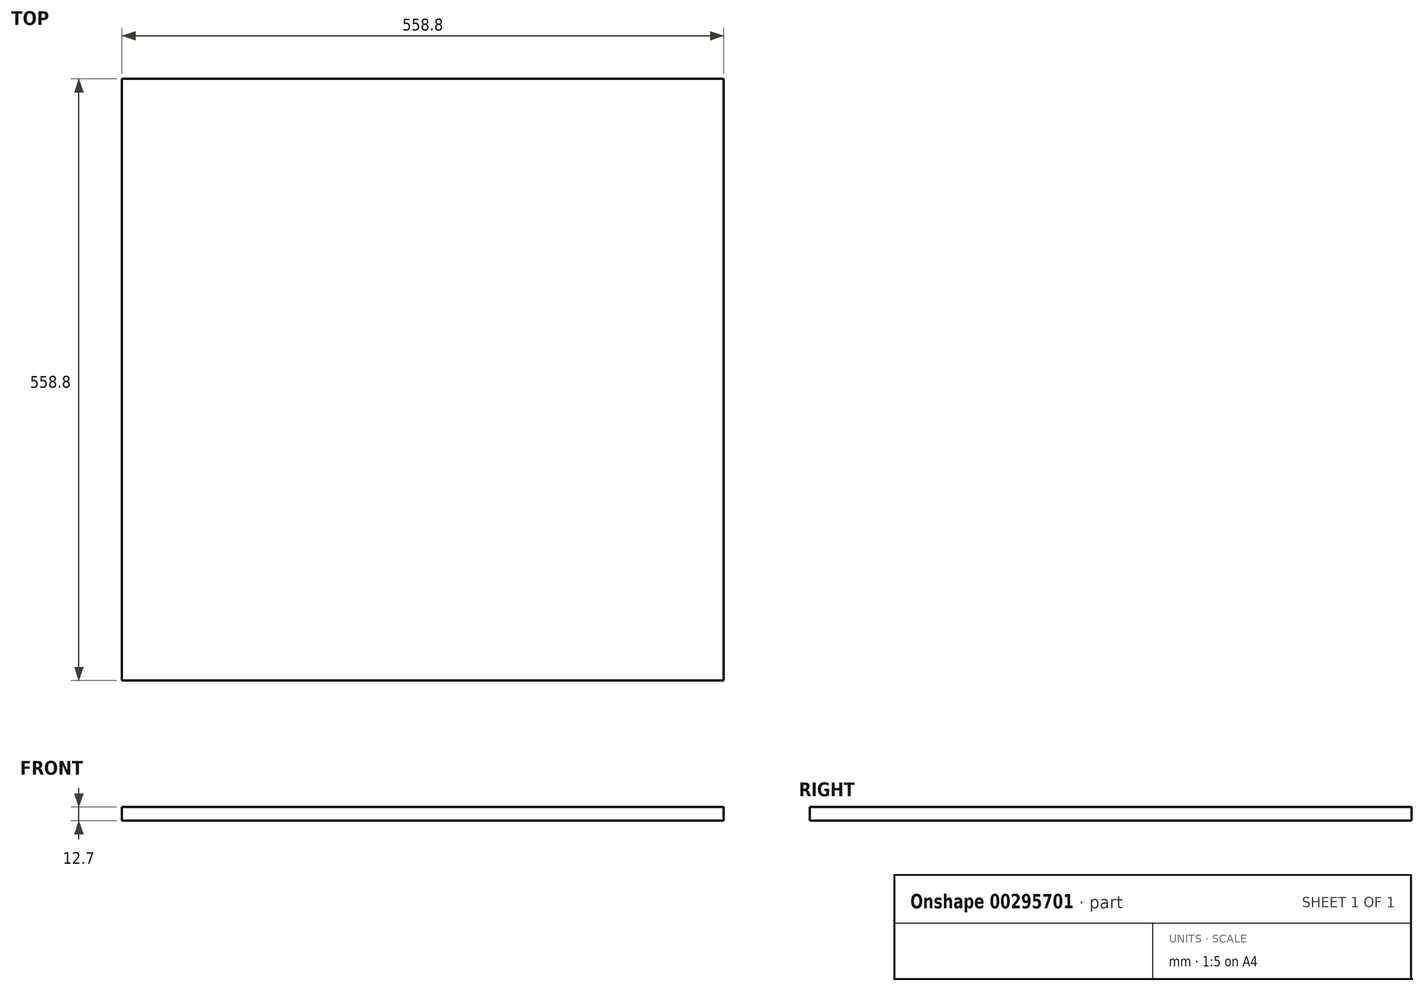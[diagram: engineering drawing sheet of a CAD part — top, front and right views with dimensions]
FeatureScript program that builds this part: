
annotation { "Feature Type Name" : "Feature", "Feature Type Description" : "" }
export const myFeature = defineFeature(function(context is Context, id is Id, definition is map)
    precondition{}
    {
        {
            var Q0;
            Q0=qCreatedBy(makeId("Top.planeOp"),FACE);
            var sketch = newSketch(context, id + "F0", { "sketchPlane" : qUnion([Q0])});
            skLineSegment(sketch, "E0.bottom", {"start": v(279.4, 279.4) * mm, "end": v(-279.4, 279.4) * mm});
            skLineSegment(sketch, "E0.top", {"start": v(279.4, -279.4) * mm, "end": v(-279.4, -279.4) * mm});
            skLineSegment(sketch, "E0.left", {"start": v(279.4, 279.4) * mm, "end": v(279.4, -279.4) * mm});
            skLineSegment(sketch, "E0.right", {"start": v(-279.4, 279.4) * mm, "end": v(-279.4, -279.4) * mm});
            skPoint(sketch, "E0.middle", {"position": v(0, 0) * mm});
            skSolve(sketch);
        }
        {
            var Q0;
            Q0 = qSketchRegion(id + "F0", true);
            extrude(context, id + "F1", {"entities" : qUnion([Q0]), "endBound" : BoundingType.SYMMETRIC, "depth" : 12.7 * mm});
        }
    });
